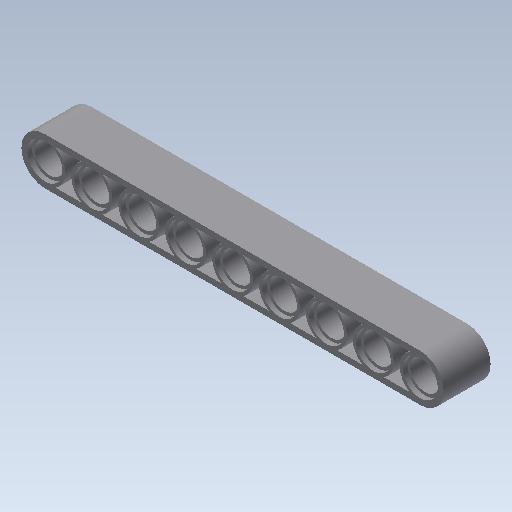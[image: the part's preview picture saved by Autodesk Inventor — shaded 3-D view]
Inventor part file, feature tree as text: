
AUTODESK INVENTOR PART (.ipt)
format: ipt  version: 2020 (Build 240168000, 168)  size: 252,416 bytes
history: native  units: mm
features: extrude x5, sketch x5
ambient origin geometry x8: Origin, YZ Plane, XZ Plane, XY Plane, X Axis, Y Axis, Z Axis, Center Point
bodies: Solid1 (feature_tree)
feature tree (10):
  extrude  "Extrusion1"  Depth=4.0mm
  extrude  "Extrusion14"  TaperAngle=0.0deg  [1 undecoded]
  extrude  "Extrusion15"  TaperAngle=180.0deg  [1 undecoded]
  extrude  "Extrusion16"  Depth=8.0mm TaperAngle=0.0deg
  extrude  "Extrusion17"  Depth=0.8mm
  sketch  "Sketch2"  dims[d0=4.0mm d1=4.0mm]
  sketch  "Sketch15"  dims[d2=64.0mm d3=0.0mm]
  sketch  "Sketch16"  dims[d4=32.0mm d9=180.0deg]
  sketch  "Sketch17"  dims[d10=0.0mm d12=8.0mm d13=0.0mm]
  sketch  "Sketch18"  dims[d141=64.0mm d142=5.0mm d143=10.0mm d145=10.0mm d146=90.0mm d148=8.0mm d150=10.0mm d151=0.0mm d152=6.0mm d153=10.0mm d155=10.0mm d156=90.0mm d158=8.0mm d160=0.8mm d161=0.0mm d162=6.0mm d163=10.0mm d165=10.0mm d166=90.0mm d168=8.0mm d170=0.8mm d171=0.0mm d172=7.0mm d173=7.0mm d174=10.0mm d176=10.0mm d177=80.0mm d179=8.0mm d181=0.8mm d182=0.0mm]
note: 2 required parameter values undecoded (feature->parameter linkage not recoverable at this tier; creation-order binding heuristic only, values carry confidence <= 0.55)
